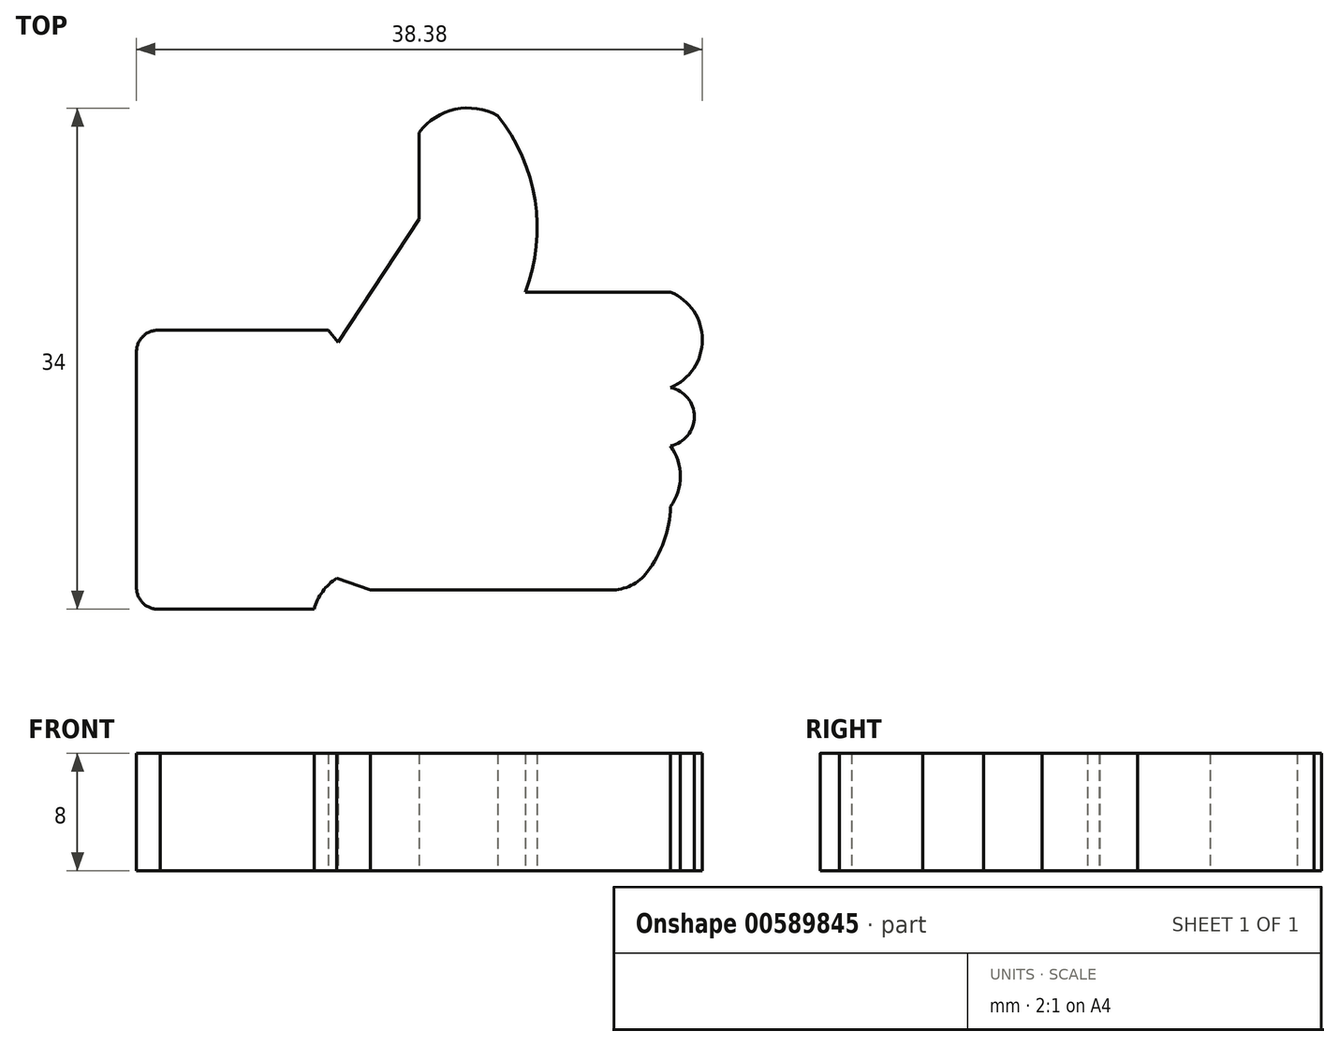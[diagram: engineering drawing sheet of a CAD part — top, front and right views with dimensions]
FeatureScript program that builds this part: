
annotation { "Feature Type Name" : "Feature", "Feature Type Description" : "" }
export const myFeature = defineFeature(function(context is Context, id is Id, definition is map)
    precondition{}
    {
        {
            var Q0;
            Q0=qCreatedBy(makeId("Top.planeOp"),FACE);
            var sketch = newSketch(context, id + "F0", { "sketchPlane" : qUnion([Q0])});
            skLineSegment(sketch, "E0", {"start": v(8.27, 20.87) * mm, "end": v(8.27, 4.86) * mm});
            skArc(sketch, "E1", {"start": v(9.89, 22.33) * mm, "mid": v(8.76, 21.96) * mm, "end": v(8.27, 20.87) * mm});
            skLineSegment(sketch, "E2", {"start": v(9.89, 22.33) * mm, "end": v(21.29, 22.33) * mm});
            skLineSegment(sketch, "E3", {"start": v(21.29, 22.33) * mm, "end": v(21.94, 21.52) * mm});
            skLineSegment(sketch, "E4", {"start": v(21.94, 21.52) * mm, "end": v(27.43, 29.85) * mm});
            skLineSegment(sketch, "E5", {"start": v(27.43, 29.85) * mm, "end": v(27.43, 35.75) * mm});
            skArc(sketch, "E6", {"start": v(32.77, 36.88) * mm, "mid": v(29.9, 37.31) * mm, "end": v(27.43, 35.75) * mm});
            skArc(sketch, "E7", {"start": v(34.63, 24.91) * mm, "mid": v(35.3, 31.15) * mm, "end": v(32.77, 36.88) * mm});
            skLineSegment(sketch, "E8", {"start": v(34.63, 24.91) * mm, "end": v(44.5, 24.91) * mm});
            skArc(sketch, "E9", {"start": v(44.5, 18.45) * mm, "mid": v(46.65, 21.68) * mm, "end": v(44.5, 24.91) * mm});
            skArc(sketch, "E10", {"start": v(44.5, 14.48) * mm, "mid": v(46.11, 16.47) * mm, "end": v(44.5, 18.45) * mm});
            skArc(sketch, "E11", {"start": v(44.5, 10.36) * mm, "mid": v(45.16, 12.42) * mm, "end": v(44.5, 14.48) * mm});
            skArc(sketch, "E12", {"start": v(41.75, 4.7) * mm, "mid": v(43.72, 7.24) * mm, "end": v(44.5, 10.36) * mm});
            skLineSegment(sketch, "E13", {"start": v(41.75, 4.7) * mm, "end": v(24.12, 4.7) * mm});
            skLineSegment(sketch, "E14", {"start": v(24.12, 4.7) * mm, "end": v(21.85, 5.5) * mm});
            skArc(sketch, "E15", {"start": v(21.85, 5.5) * mm, "mid": v(20.9, 4.6) * mm, "end": v(20.32, 3.4) * mm});
            skLineSegment(sketch, "E16", {"start": v(20.32, 3.4) * mm, "end": v(9.89, 3.4) * mm});
            skArc(sketch, "E17", {"start": v(8.27, 4.86) * mm, "mid": v(8.76, 3.77) * mm, "end": v(9.89, 3.4) * mm});
            skSolve(sketch);
        }
        {
            var Q0;
            Q0=makeQuery(id+"F0.imprint","IMPRINT",FACE,{"disambiguationData":[TD([[makeQuery(id+"F0.imprint","IMPRINT",EDGE,{"derivedFrom":sQuery(id+"F0.wireOp",EDGE,"E0")}),1.0]])]});
            extrude(context, id + "F1", {"entities" : qUnion([Q0]), "depth" : 8 * mm, "offsetDistance" : 25 * mm});
        }
        {
            var Q0;
            Q0=makeQuery(id+"F1.opExtrude","SWEPT_EDGE",EDGE,{"disambiguationData":[OSD([sQuery(id+"F0.wireOp",EDGE,"E12"),sQuery(id+"F0.wireOp",EDGE,"E13")])]});
            fillet(context, id + "F2", {"entities" : qUnion([Q0]), "radius" : 3.1 * mm, "tangentPropagation" : true, "allowEdgeOverflow" : false});
        }
    });
